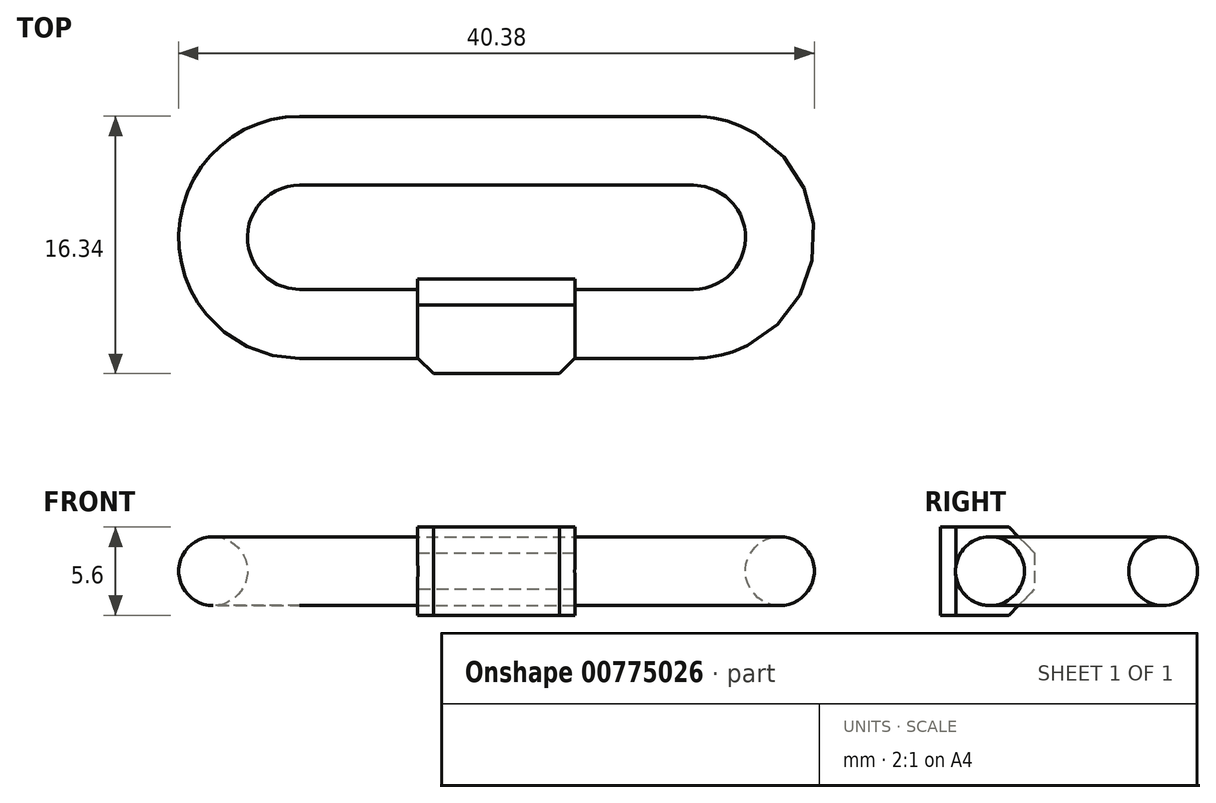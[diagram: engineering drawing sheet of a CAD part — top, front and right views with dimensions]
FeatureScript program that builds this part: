
annotation { "Feature Type Name" : "Feature", "Feature Type Description" : "" }
export const myFeature = defineFeature(function(context is Context, id is Id, definition is map)
    precondition{}
    {
        {
            var Q0;
            Q0=qCreatedBy(makeId("Top.planeOp"),FACE);
            var sketch = newSketch(context, id + "F0", { "sketchPlane" : qUnion([Q0])});
            skLineSegment(sketch, "E0", {"start": v(-25, 11) * mm, "end": v(0, 11) * mm});
            skLineSegment(sketch, "E1.top", {"start": v(-25, 0) * mm, "end": v(0, 0) * mm});
            skArc(sketch, "E2", {"start": v(-25, 11) * mm, "mid": v(-30.5, 5.5) * mm, "end": v(-25, 0) * mm});
            skArc(sketch, "E3", {"start": v(0, 0) * mm, "mid": v(5.5, 5.5) * mm, "end": v(0, 11) * mm});
            skSolve(sketch);
        }
        {
            var Q0;
            Q0=qCreatedBy(makeId("Right.planeOp"),FACE);
            var sketch = newSketch(context, id + "F1", { "sketchPlane" : qUnion([Q0])});
            skPoint(sketch, "E4.0", {"position": v(0, 0) * mm});
            skCircle(sketch, "E5", {"center": v(0, 0) * mm, "radius": 2.19 * mm});
            skSolve(sketch);
        }
        {
            var Q0;
            Q0=makeQuery(id+"F1.imprint","IMPRINT",FACE,{"disambiguationData":[TD([[makeQuery(id+"F1.imprint","IMPRINT",EDGE,{"derivedFrom":sQuery(id+"F1.wireOp",EDGE,"E5")}),1.0]])]});
            var Q1;
            Q1=sQuery(id+"F0.wireOp",EDGE,"E3");
            var Q2;
            Q2=sQuery(id+"F0.wireOp",EDGE,"E0");
            var Q3;
            Q3=sQuery(id+"F0.wireOp",EDGE,"E2");
            var Q4;
            Q4=sQuery(id+"F0.wireOp",EDGE,"E1.top");
            sweep(context, id + "F2", {"profiles" : qUnion([Q0]), "path" : qUnion([Q1, Q2, Q3, Q4])});
        }
        {
            var Q0;
            Q0=qCreatedBy(makeId("Top.planeOp"),FACE);
            var sketch = newSketch(context, id + "F3", { "sketchPlane" : qUnion([Q0])});
            skLineSegment(sketch, "E6.bottom", {"start": v(-17.5, 2.84) * mm, "end": v(-7.5, 2.84) * mm});
            skLineSegment(sketch, "E6.top", {"start": v(-17.5, -3.15) * mm, "end": v(-7.5, -3.15) * mm});
            skLineSegment(sketch, "E6.left", {"start": v(-17.5, 2.84) * mm, "end": v(-17.5, -3.15) * mm});
            skLineSegment(sketch, "E6.right", {"start": v(-7.5, 2.84) * mm, "end": v(-7.5, -3.15) * mm});
            skLineSegment(sketch, "E7.bottom", {"start": v(-17.5, -3.15) * mm, "end": v(-14.5, -3.15) * mm});
            skLineSegment(sketch, "E7.top", {"start": v(-17.5, -8.51) * mm, "end": v(-14.5, -8.51) * mm});
            skLineSegment(sketch, "E7.left", {"start": v(-17.5, -3.15) * mm, "end": v(-17.5, -8.51) * mm});
            skLineSegment(sketch, "E7.right", {"start": v(-14.5, -3.15) * mm, "end": v(-14.5, -8.51) * mm});
            skLineSegment(sketch, "E8.bottom", {"start": v(-7.5, -3.15) * mm, "end": v(-10.5, -3.15) * mm});
            skLineSegment(sketch, "E8.top", {"start": v(-7.5, -8.51) * mm, "end": v(-10.5, -8.51) * mm});
            skLineSegment(sketch, "E8.left", {"start": v(-7.5, -3.15) * mm, "end": v(-7.5, -8.51) * mm});
            skLineSegment(sketch, "E8.right", {"start": v(-10.5, -3.15) * mm, "end": v(-10.5, -8.51) * mm});
            skSolve(sketch);
        }
        {
            var Q0;
            Q0=makeQuery(id+"F3.imprint","IMPRINT",FACE,{"disambiguationData":[TD([[makeQuery(id+"F3.imprint","IMPRINT",EDGE,{"derivedFrom":sQuery(id+"F3.wireOp",EDGE,"E6.bottom")}),-1.0]])]});
            var Q1;
            Q1=makeQuery(id+"F3.imprint","IMPRINT",FACE,{"disambiguationData":[TD([[makeQuery(id+"F3.imprint","IMPRINT",EDGE,{"derivedFrom":sQuery(id+"F3.wireOp",EDGE,"E7.bottom")}),-1.0]])]});
            var Q2;
            Q2=makeQuery(id+"F3.imprint","IMPRINT",FACE,{"disambiguationData":[TD([[makeQuery(id+"F3.imprint","IMPRINT",EDGE,{"derivedFrom":sQuery(id+"F3.wireOp",EDGE,"E8.bottom")}),1.0]])]});
            extrude(context, id + "F4", {"entities" : qUnion([Q0, Q1, Q2]), "operationType" : NewBodyOperationType.ADD, "endBound" : BoundingType.SYMMETRIC, "depth" : 5.6 * mm, "offsetDistance" : 25 * mm});
        }
        {
            var Q0;
            Q0=makeQuery(id+"F4.opExtrude","CAP_EDGE",EDGE,{"disambiguationData":[OSD([sQuery(id+"F3.wireOp",EDGE,"E6.bottom")])],"isStart":false});
            var Q1;
            Q1=makeQuery(id+"F4.opExtrude","CAP_EDGE",EDGE,{"disambiguationData":[OSD([sQuery(id+"F3.wireOp",EDGE,"E6.bottom")])],"isStart":true});
            chamfer(context, id + "F5", {"entities" : qUnion([Q0, Q1]), "width" : 1.65 * mm, "tangentPropagation" : true});
        }
        {
            var Q0;
            Q0=makeQuery(id+"F4.opExtrude","CAP_EDGE",EDGE,{"disambiguationData":[OSD([sQuery(id+"F3.wireOp",EDGE,"E8.top")])],"isStart":true});
            var Q1;
            Q1=makeQuery(id+"F4.opExtrude","SWEPT_EDGE",EDGE,{"disambiguationData":[OSD([sQuery(id+"F3.wireOp",EDGE,"E8.top"),sQuery(id+"F3.wireOp",EDGE,"E8.left")])]});
            var Q2;
            Q2=makeQuery(id+"F4.opExtrude","CAP_EDGE",EDGE,{"disambiguationData":[OSD([sQuery(id+"F3.wireOp",EDGE,"E8.top")])],"isStart":false});
            var Q3;
            Q3=makeQuery(id+"F4.opExtrude","CAP_EDGE",EDGE,{"disambiguationData":[OSD([sQuery(id+"F3.wireOp",EDGE,"E7.top")])],"isStart":true});
            var Q4;
            Q4=makeQuery(id+"F4.opExtrude","SWEPT_EDGE",EDGE,{"disambiguationData":[OSD([sQuery(id+"F3.wireOp",EDGE,"E7.top"),sQuery(id+"F3.wireOp",EDGE,"E7.left")])]});
            var Q5;
            Q5=makeQuery(id+"F4.opExtrude","CAP_EDGE",EDGE,{"disambiguationData":[OSD([sQuery(id+"F3.wireOp",EDGE,"E7.top")])],"isStart":false});
            chamfer(context, id + "F6", {"entities" : qUnion([Q0, Q1, Q2, Q3, Q4, Q5]), "width" : 1 * mm, "tangentPropagation" : true});
        }
    });
